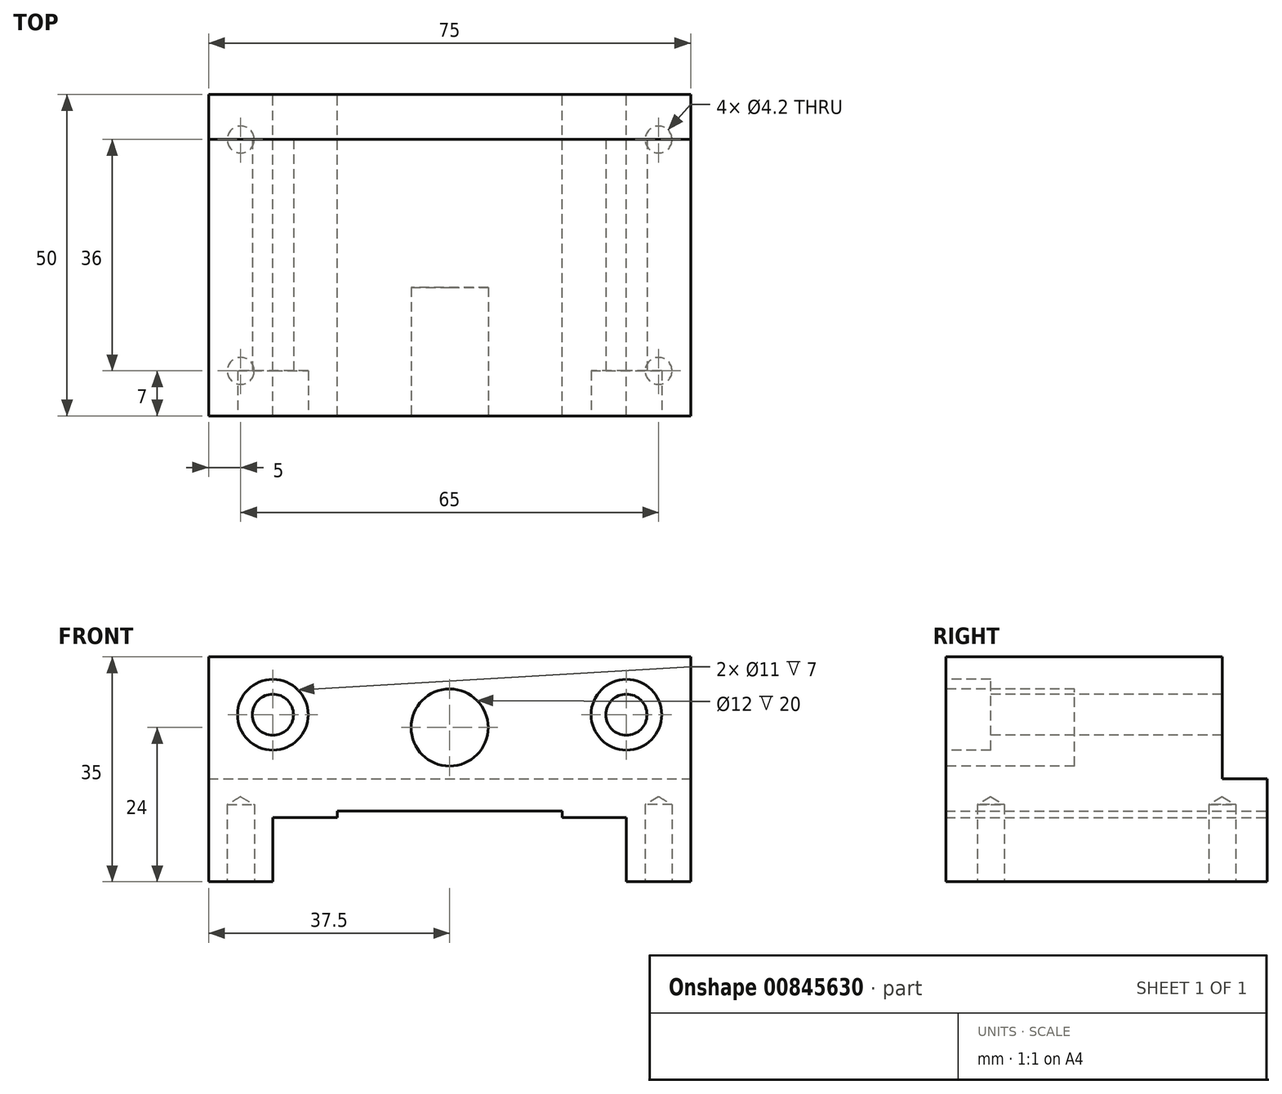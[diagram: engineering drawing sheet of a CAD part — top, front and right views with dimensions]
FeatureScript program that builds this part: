
annotation { "Feature Type Name" : "Feature", "Feature Type Description" : "" }
export const myFeature = defineFeature(function(context is Context, id is Id, definition is map)
    precondition{}
    {
        {
            var Q0;
            Q0=qCreatedBy(makeId("Front.planeOp"),FACE);
            var sketch = newSketch(context, id + "F0", { "sketchPlane" : qUnion([Q0])});
            skLineSegment(sketch, "E0", {"start": v(0, 0) * mm, "end": v(-17.5, 0) * mm});
            skLineSegment(sketch, "E1", {"start": v(-17.5, 0) * mm, "end": v(-17.5, -1) * mm});
            skLineSegment(sketch, "E2", {"start": v(-17.5, -1) * mm, "end": v(-27.5, -1) * mm});
            skLineSegment(sketch, "E3", {"start": v(-27.5, -1) * mm, "end": v(-27.5, -11) * mm});
            skLineSegment(sketch, "E4", {"start": v(-27.5, -11) * mm, "end": v(-37.5, -11) * mm});
            skLineSegment(sketch, "E5", {"start": v(-37.5, -11) * mm, "end": v(-37.5, 24) * mm});
            skLineSegment(sketch, "E6", {"start": v(-37.5, 24) * mm, "end": v(0, 24) * mm});
            skLineSegment(sketch, "E7", {"start": v(0, 24) * mm, "end": v(0, 0) * mm});
            skSolve(sketch);
        }
        {
            var Q0;
            Q0=makeQuery(id+"F0.imprint","IMPRINT",FACE,{"disambiguationData":[TD([[makeQuery(id+"F0.imprint","IMPRINT",EDGE,{"derivedFrom":sQuery(id+"F0.wireOp",EDGE,"E0")}),-1.0]])]});
            extrude(context, id + "F1", {"entities" : qUnion([Q0]), "endBound" : BoundingType.SYMMETRIC, "depth" : 50 * mm, "offsetDistance" : 25 * mm});
        }
        {
            var Q0;
            Q0=qCreatedBy(makeId("Right.planeOp"),FACE);
            var sketch = newSketch(context, id + "F2", { "sketchPlane" : qUnion([Q0])});
            skLineSegment(sketch, "E8.bottom", {"start": v(25, 24) * mm, "end": v(18, 24) * mm});
            skLineSegment(sketch, "E8.top", {"start": v(25, 5) * mm, "end": v(18, 5) * mm});
            skLineSegment(sketch, "E8.left", {"start": v(25, 24) * mm, "end": v(25, 5) * mm});
            skLineSegment(sketch, "E8.right", {"start": v(18, 24) * mm, "end": v(18, 5) * mm});
            skSolve(sketch);
        }
        {
            var Q0;
            Q0=makeQuery(id+"F2.imprint","IMPRINT",FACE,{"disambiguationData":[TD([[makeQuery(id+"F2.imprint","IMPRINT",EDGE,{"derivedFrom":sQuery(id+"F2.wireOp",EDGE,"E8.bottom")}),1.0]])]});
            extrude(context, id + "F3", {"entities" : qUnion([Q0]), "operationType" : NewBodyOperationType.REMOVE, "endBound" : BoundingType.THROUGH_ALL, "oppositeDirection" : true, "depth" : 25 * mm, "offsetDistance" : 25 * mm});
        }
        {
            var Q0;
            Q0=makeQuery(id+"F1.opExtrude","SWEPT_FACE",FACE,{"disambiguationData":[OSD([sQuery(id+"F0.wireOp",EDGE,"E4")])]});
            var sketch = newSketch(context, id + "F4", { "sketchPlane" : qUnion([Q0])});
            skLineSegment(sketch, "E9", {"start": v(-32.5, 18) * mm, "end": v(-32.5, -18) * mm, "construction": true});
            skSolve(sketch);
        }
        {
            var Q0;
            Q0=sQuery(id+"F4.wireOp",VERTEX,"E9.start");
            var Q1;
            Q1=sQuery(id+"F4.wireOp",VERTEX,"E9.end");
            var Q2;
            Q2=makeQuery(id+"F1.opExtrude","SWEPT_BODY",BODY,{"disambiguationData":[OSD([sQuery(id+"F0.wireOp",EDGE,"E0"),sQuery(id+"F0.wireOp",EDGE,"E1"),sQuery(id+"F0.wireOp",EDGE,"E2"),sQuery(id+"F0.wireOp",EDGE,"E3"),sQuery(id+"F0.wireOp",EDGE,"E4"),sQuery(id+"F0.wireOp",EDGE,"E5"),sQuery(id+"F0.wireOp",EDGE,"E6"),sQuery(id+"F0.wireOp",EDGE,"E7")])]});
            hole(context, id + "F5", {"style" : HoleStyle.SIMPLE, "endStyle" : HoleEndStyle.BLIND, "standardTappedOrClearance" : lookupTablePath({ "standard" : "ISO", "engagement" : "75%", "pitch" : "0.8 mm", "size" : "M5", "type" : "Tapped" }), "standardBlindInLast" : lookupTablePath({ "standard" : "ISO", "engagement" : "75%", "pitch" : "0.8 mm", "size" : "M5", "type" : "Tapped" }), "holeDiameter" : 4.2 * mm, "majorDiameter" : 5 * mm, "showTappedDepth" : true, "holeDepth" : 12 * mm, "isTappedThrough" : true, "tappedDepth" : 10.4 * mm, "tapClearance" : 2, "startFromSketch" : true, "locations" : qUnion([Q0, Q1]), "scope" : qUnion([Q2])});
        }
        {
            var Q0;
            Q0=makeQuery(id+"F1.opExtrude","CAP_FACE",FACE,{"disambiguationData":[OSD([sQuery(id+"F0.wireOp",EDGE,"E0"),sQuery(id+"F0.wireOp",EDGE,"E1"),sQuery(id+"F0.wireOp",EDGE,"E2"),sQuery(id+"F0.wireOp",EDGE,"E3"),sQuery(id+"F0.wireOp",EDGE,"E4"),sQuery(id+"F0.wireOp",EDGE,"E5"),sQuery(id+"F0.wireOp",EDGE,"E6"),sQuery(id+"F0.wireOp",EDGE,"E7")])],"isStart":false});
            var sketch = newSketch(context, id + "F6", { "sketchPlane" : qUnion([Q0])});
            skPoint(sketch, "E10", {"position": v(-27.5, 15) * mm});
            skSolve(sketch);
        }
        {
            var Q0;
            Q0=sQuery(id+"F6.wireOp",VERTEX,"E10");
            var Q1;
            Q1=makeQuery(id+"F1.opExtrude","SWEPT_BODY",BODY,{"disambiguationData":[OSD([sQuery(id+"F0.wireOp",EDGE,"E0"),sQuery(id+"F0.wireOp",EDGE,"E1"),sQuery(id+"F0.wireOp",EDGE,"E2"),sQuery(id+"F0.wireOp",EDGE,"E3"),sQuery(id+"F0.wireOp",EDGE,"E4"),sQuery(id+"F0.wireOp",EDGE,"E5"),sQuery(id+"F0.wireOp",EDGE,"E6"),sQuery(id+"F0.wireOp",EDGE,"E7")])]});
            hole(context, id + "F7", {"style" : HoleStyle.C_BORE, "endStyle" : HoleEndStyle.THROUGH, "holeDiameter" : 6.4 * mm, "cBoreDiameter" : 11 * mm, "cBoreDepth" : 7 * mm, "majorDiameter" : 5 * mm, "isTappedThrough" : true, "tappedDepth" : 9.6 * mm, "tapClearance" : 3, "startFromSketch" : true, "locations" : qUnion([Q0]), "scope" : qUnion([Q1])});
        }
        {
            var Q0;
            Q0=makeQuery(id+"F1.opExtrude","SWEPT_BODY",BODY,{"disambiguationData":[OSD([sQuery(id+"F0.wireOp",EDGE,"E0"),sQuery(id+"F0.wireOp",EDGE,"E1"),sQuery(id+"F0.wireOp",EDGE,"E2"),sQuery(id+"F0.wireOp",EDGE,"E3"),sQuery(id+"F0.wireOp",EDGE,"E4"),sQuery(id+"F0.wireOp",EDGE,"E5"),sQuery(id+"F0.wireOp",EDGE,"E6"),sQuery(id+"F0.wireOp",EDGE,"E7")])]});
            var Q1;
            Q1=qCreatedBy(makeId("Right.planeOp"),FACE);
            mirror(context, id + "F8", {"operationType" : NewBodyOperationType.ADD, "entities" : qUnion([Q0]), "mirrorPlane" : qUnion([Q1])});
        }
        {
            var Q0;
            {var subQ0=makeQuery(id+"F1.opExtrude","CAP_FACE",FACE,{"disambiguationData":[OSD([sQuery(id+"F0.wireOp",EDGE,"E0"),sQuery(id+"F0.wireOp",EDGE,"E1"),sQuery(id+"F0.wireOp",EDGE,"E2"),sQuery(id+"F0.wireOp",EDGE,"E3"),sQuery(id+"F0.wireOp",EDGE,"E4"),sQuery(id+"F0.wireOp",EDGE,"E5"),sQuery(id+"F0.wireOp",EDGE,"E6"),sQuery(id+"F0.wireOp",EDGE,"E7")])],"isStart":false});Q0=makeQuery(id+"F8.boolean.opBoolean","MERGE",FACE,{"derivedFrom":[subQ0,makeQuery(id+"F8.opPattern","COPY",FACE,{"derivedFrom":subQ0,"instanceName":"1"})]});}
            var sketch = newSketch(context, id + "F9", { "sketchPlane" : qUnion([Q0])});
            skCircle(sketch, "E11", {"center": v(0, 13) * mm, "radius": 6 * mm});
            skSolve(sketch);
        }
        {
            var Q0;
            Q0=makeQuery(id+"F9.imprint","IMPRINT",FACE,{"disambiguationData":[TD([[makeQuery(id+"F9.imprint","IMPRINT",EDGE,{"derivedFrom":sQuery(id+"F9.wireOp",EDGE,"E11")}),1.0]])]});
            extrude(context, id + "F10", {"entities" : qUnion([Q0]), "operationType" : NewBodyOperationType.REMOVE, "oppositeDirection" : true, "depth" : 20 * mm, "offsetDistance" : 25 * mm});
        }
    });
